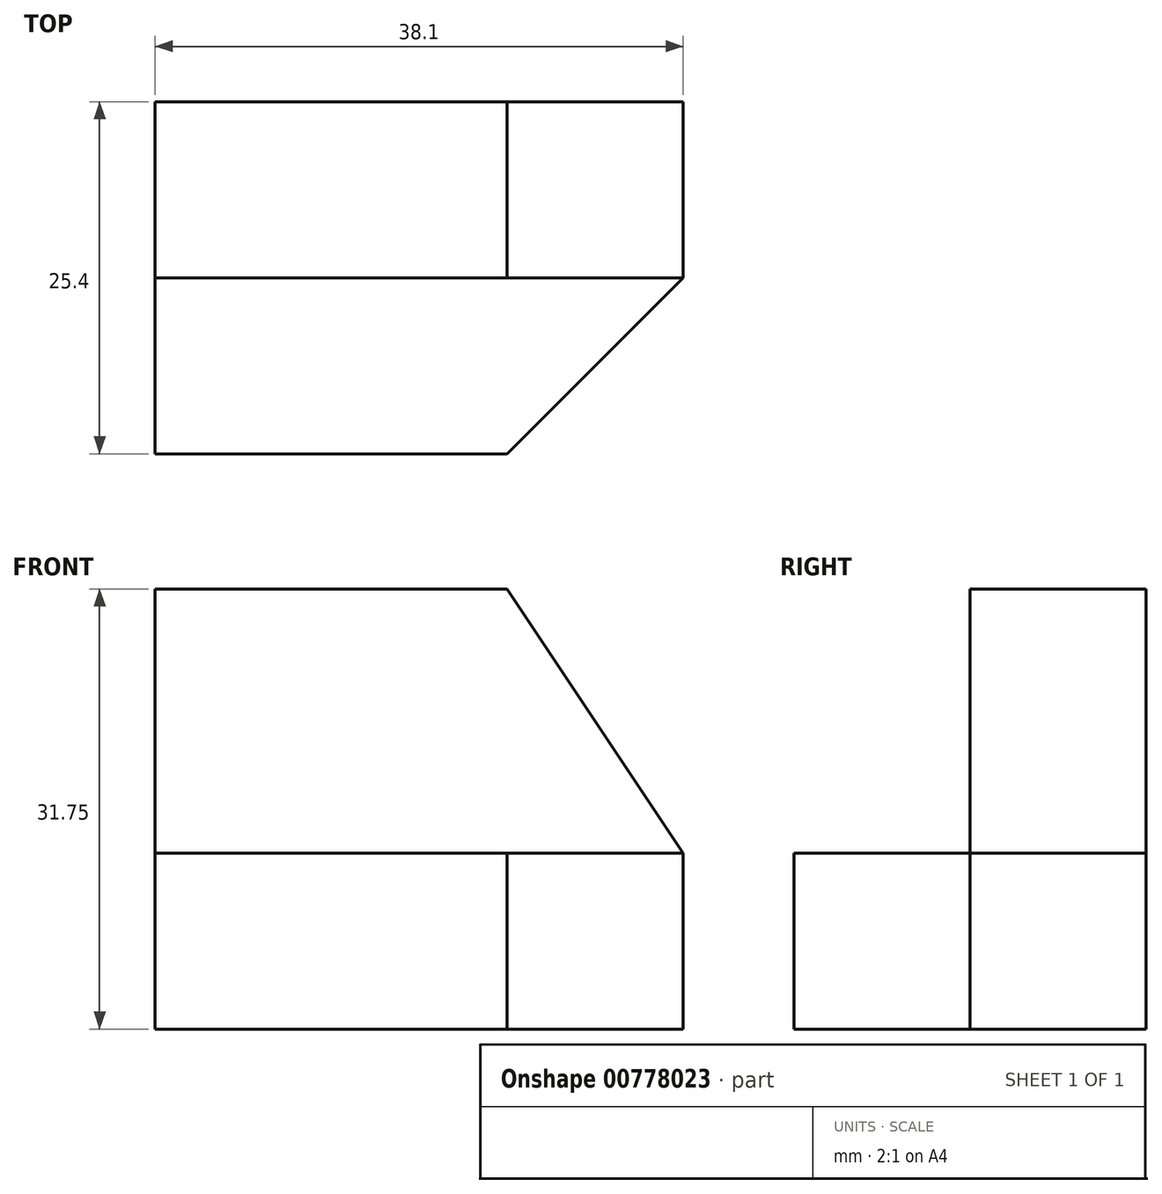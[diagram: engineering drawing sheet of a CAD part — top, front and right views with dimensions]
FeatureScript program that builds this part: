
annotation { "Feature Type Name" : "Feature", "Feature Type Description" : "" }
export const myFeature = defineFeature(function(context is Context, id is Id, definition is map)
    precondition{}
    {
        {
            var Q0;
            Q0=qCreatedBy(makeId("Front.planeOp"),FACE);
            var sketch = newSketch(context, id + "F0", { "sketchPlane" : qUnion([Q0])});
            skLineSegment(sketch, "E0", {"start": v(0, 0) * mm, "end": v(38.1, 0) * mm});
            skLineSegment(sketch, "E1", {"start": v(38.1, 0) * mm, "end": v(38.1, 31.75) * mm});
            skLineSegment(sketch, "E2", {"start": v(38.1, 31.75) * mm, "end": v(0, 31.75) * mm});
            skLineSegment(sketch, "E3", {"start": v(0, 31.75) * mm, "end": v(0, 0) * mm});
            skSolve(sketch);
        }
        {
            var Q0;
            Q0=makeQuery(id+"F0.imprint","IMPRINT",FACE,{"disambiguationData":[TD([[makeQuery(id+"F0.imprint","IMPRINT",EDGE,{"derivedFrom":sQuery(id+"F0.wireOp",EDGE,"E0")}),1.0]])]});
            extrude(context, id + "F1", {"entities" : qUnion([Q0]), "depth" : 25.4 * mm, "offsetDistance" : 25.4 * mm});
        }
        {
            var Q0;
            Q0=makeQuery(id+"F1.opExtrude","SWEPT_FACE",FACE,{"disambiguationData":[OSD([sQuery(id+"F0.wireOp",EDGE,"E1")])]});
            var sketch = newSketch(context, id + "F2", { "sketchPlane" : qUnion([Q0])});
            skLineSegment(sketch, "E4", {"start": v(0, 31.75) * mm, "end": v(-12.7, 31.75) * mm});
            skLineSegment(sketch, "E5", {"start": v(-12.7, 31.75) * mm, "end": v(-12.7, 12.7) * mm});
            skLineSegment(sketch, "E6", {"start": v(-12.7, 12.7) * mm, "end": v(-25.4, 12.7) * mm});
            skSolve(sketch);
        }
        {
            var Q0;
            {var subQ0=sQuery(id+"F2.wireOp",EDGE,"E5");Q0=makeQuery(id+"F2.imprint","IMPRINT",FACE,{"disambiguationData":[TD([[makeQuery(id+"F2.imprint","IMPRINT",EDGE,{"derivedFrom":subQ0}),-1.0]])]});}
            extrude(context, id + "F3", {"entities" : qUnion([Q0]), "operationType" : NewBodyOperationType.REMOVE, "oppositeDirection" : true, "depth" : 38.1 * mm, "offsetDistance" : 25.4 * mm});
        }
        {
            var Q0;
            Q0=makeQuery(id+"F3.boolean.opBoolean","COPY",FACE,{"derivedFrom":makeQuery(id+"F3.opExtrude","SWEPT_FACE",FACE,{"disambiguationData":[OSD([sQuery(id+"F2.wireOp",EDGE,"E5")])]})});
            var sketch = newSketch(context, id + "F4", { "sketchPlane" : qUnion([Q0])});
            skLineSegment(sketch, "E7", {"start": v(0, 31.75) * mm, "end": v(25.4, 31.75) * mm});
            skLineSegment(sketch, "E8", {"start": v(25.4, 31.75) * mm, "end": v(38.1, 12.7) * mm});
            skSolve(sketch);
        }
        {
            var Q0;
            {var subQ0=sQuery(id+"F4.wireOp",EDGE,"E8");Q0=makeQuery(id+"F4.imprint","IMPRINT",FACE,{"disambiguationData":[TD([[makeQuery(id+"F4.imprint","IMPRINT",EDGE,{"derivedFrom":subQ0}),1.0]])]});}
            extrude(context, id + "F5", {"entities" : qUnion([Q0]), "operationType" : NewBodyOperationType.REMOVE, "oppositeDirection" : true, "depth" : 25.4 * mm, "offsetDistance" : 25.4 * mm});
        }
        {
            var Q0;
            Q0=makeQuery(id+"F3.boolean.opBoolean","COPY",FACE,{"derivedFrom":makeQuery(id+"F3.opExtrude","SWEPT_FACE",FACE,{"disambiguationData":[OSD([sQuery(id+"F2.wireOp",EDGE,"E6")])]})});
            var sketch = newSketch(context, id + "F6", { "sketchPlane" : qUnion([Q0])});
            skLineSegment(sketch, "E9", {"start": v(0, -25.4) * mm, "end": v(25.4, -25.4) * mm});
            skLineSegment(sketch, "E10", {"start": v(25.4, -25.4) * mm, "end": v(38.1, -12.7) * mm});
            skSolve(sketch);
        }
        {
            var Q0;
            {var subQ0=sQuery(id+"F6.wireOp",EDGE,"E10");Q0=makeQuery(id+"F6.imprint","IMPRINT",FACE,{"disambiguationData":[TD([[makeQuery(id+"F6.imprint","IMPRINT",EDGE,{"derivedFrom":subQ0}),-1.0]])]});}
            extrude(context, id + "F7", {"entities" : qUnion([Q0]), "operationType" : NewBodyOperationType.REMOVE, "oppositeDirection" : true, "depth" : 12.7 * mm, "offsetDistance" : 25.4 * mm});
        }
    });
